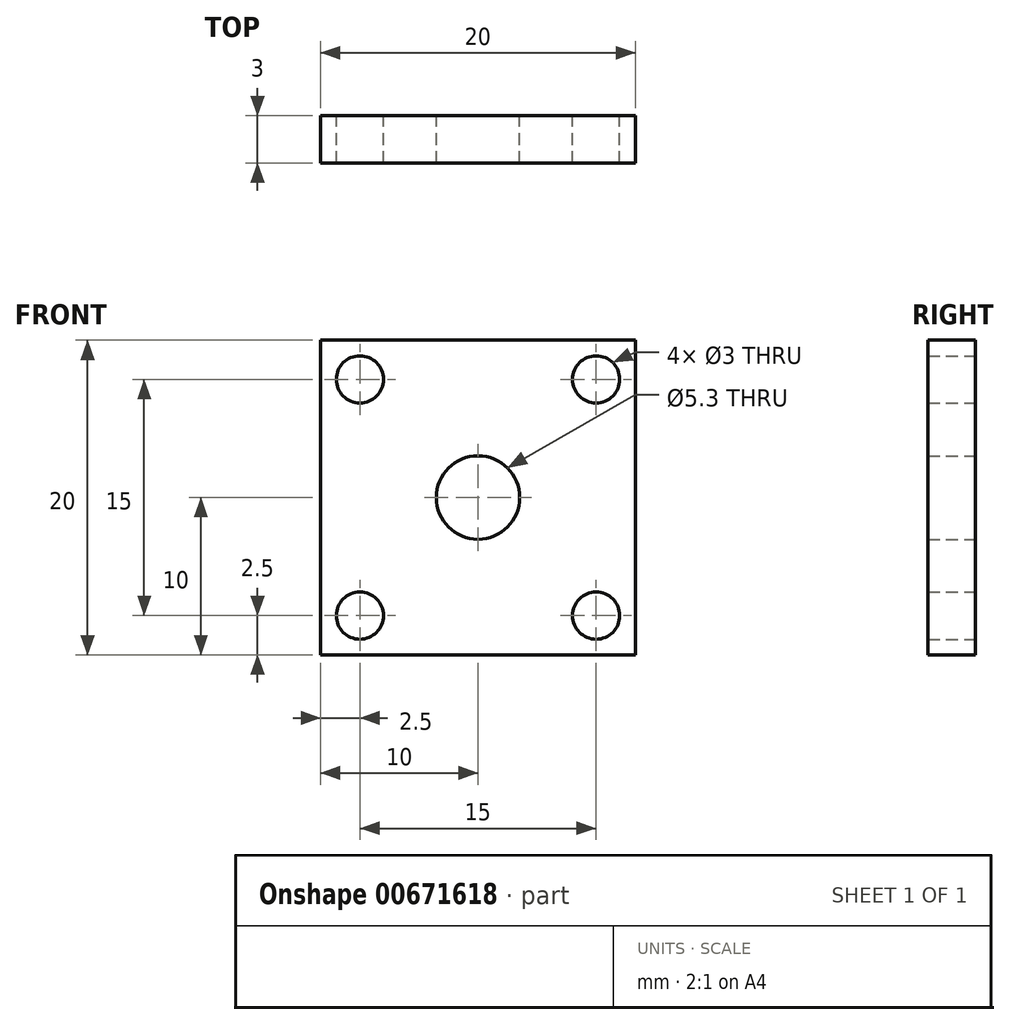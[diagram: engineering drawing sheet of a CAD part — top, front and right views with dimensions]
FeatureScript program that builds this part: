
annotation { "Feature Type Name" : "Feature", "Feature Type Description" : "" }
export const myFeature = defineFeature(function(context is Context, id is Id, definition is map)
    precondition{}
    {
        {
            var Q0;
            Q0=qCreatedBy(makeId("Front.planeOp"),FACE);
            var sketch = newSketch(context, id + "F0", { "sketchPlane" : qUnion([Q0])});
            skCircle(sketch, "E0", {"center": v(-7.5, 7.5) * mm, "radius": 1.5 * mm});
            skCircle(sketch, "E1.0.1.0", {"center": v(-7.5, -7.5) * mm, "radius": 1.5 * mm});
            skCircle(sketch, "E1.1.0.0", {"center": v(7.5, 7.5) * mm, "radius": 1.5 * mm});
            skCircle(sketch, "E1.1.1.0", {"center": v(7.5, -7.5) * mm, "radius": 1.5 * mm});
            skLineSegment(sketch, "E1.direction1", {"start": v(-7.5, 7.5) * mm, "end": v(7.5, 7.5) * mm, "construction": true});
            skLineSegment(sketch, "E1.direction2", {"start": v(-7.5, 7.5) * mm, "end": v(-7.5, -7.5) * mm, "construction": true});
            skLineSegment(sketch, "E2", {"start": v(7.5, 7.5) * mm, "end": v(-7.5, -7.5) * mm, "construction": true});
            skCircle(sketch, "E3", {"center": v(0, 0) * mm, "radius": 2.65 * mm});
            skLineSegment(sketch, "E4.bottom", {"start": v(-10, 10) * mm, "end": v(10, 10) * mm});
            skLineSegment(sketch, "E4.top", {"start": v(-10, -10) * mm, "end": v(10, -10) * mm});
            skLineSegment(sketch, "E4.left", {"start": v(-10, 10) * mm, "end": v(-10, -10) * mm});
            skLineSegment(sketch, "E4.right", {"start": v(10, 10) * mm, "end": v(10, -10) * mm});
            skLineSegment(sketch, "E5", {"start": v(-10, 10) * mm, "end": v(10, -10) * mm, "construction": true});
            skSolve(sketch);
        }
        {
            var Q0;
            Q0=makeQuery(id+"F0.imprint","IMPRINT",FACE,{"disambiguationData":[TD([[makeQuery(id+"F0.imprint","IMPRINT",EDGE,{"derivedFrom":sQuery(id+"F0.wireOp",EDGE,"E0")}),-1.0]])]});
            extrude(context, id + "F1", {"entities" : qUnion([Q0]), "endBound" : BoundingType.SYMMETRIC, "depth" : 3 * mm, "offsetDistance" : 25 * mm});
        }
    });
